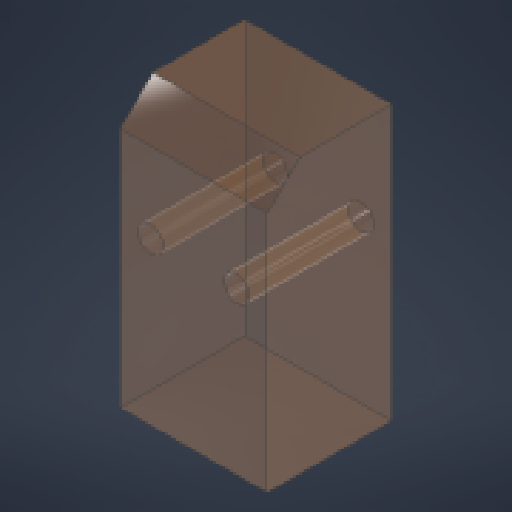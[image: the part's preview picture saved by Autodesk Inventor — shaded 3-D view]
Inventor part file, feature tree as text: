
AUTODESK INVENTOR PART (.ipt)
format: ipt  version: 2025 (Build 290162000, 162)  size: 219,648 bytes
history: native  units: mm
features: extrude x1, chamfer x1, sketch x1, other x1
ambient origin geometry x8: Origin, YZ Plane, XZ Plane, XY Plane, X Axis, Y Axis, Z Axis, Center Point
bodies: Solid1 (feature_tree)
feature tree (4):
  extrude  "Extrusion1"  Depth=33.79mm
  chamfer  "Chamfer1"  Distance=13.9mm
  sketch  "Sketch1"  dims[d0=18.1mm d1=33.79mm d2=13.9mm d3=5.29mm d4=10.58mm d5=3.15mm d6=3.15mm d7=15.3mm d8=0.0mm d9=4.0mm d10=2.0mm d11=45.0deg]
  other  "Finish1"
